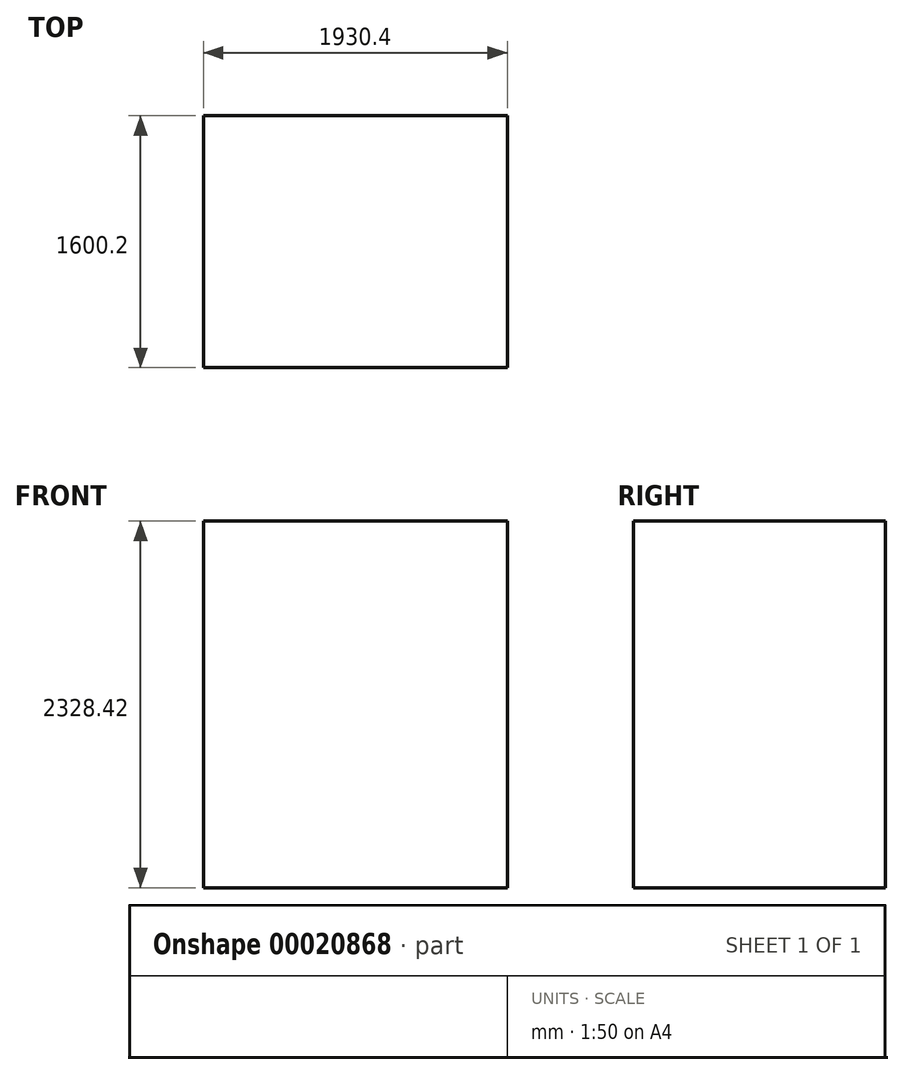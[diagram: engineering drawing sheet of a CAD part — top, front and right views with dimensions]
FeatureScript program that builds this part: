
annotation { "Feature Type Name" : "Feature", "Feature Type Description" : "" }
export const myFeature = defineFeature(function(context is Context, id is Id, definition is map)
    precondition{}
    {
        {
            var Q0;
            Q0=qCreatedBy(makeId("Top.planeOp"),FACE);
            var sketch = newSketch(context, id + "F0", { "sketchPlane" : qUnion([Q0])});
            skLineSegment(sketch, "E0", {"start": v(0, 0) * mm, "end": v(-1930.4, 0) * mm});
            skLineSegment(sketch, "E1", {"start": v(-1930.4, 0) * mm, "end": v(-1930.4, -1600.2) * mm});
            skLineSegment(sketch, "E2", {"start": v(-1930.4, -1600.2) * mm, "end": v(0, -1600.2) * mm});
            skLineSegment(sketch, "E3", {"start": v(0, 0) * mm, "end": v(0, -1600.2) * mm});
            skSolve(sketch);
        }
        {
            var Q0;
            Q0=makeQuery(id+"F0.imprint","IMPRINT",FACE,{"disambiguationData":[TD([[makeQuery(id+"F0.imprint","IMPRINT",EDGE,{"derivedFrom":sQuery(id+"F0.wireOp",EDGE,"E0")}),1.0]])]});
            extrude(context, id + "F1", {"entities" : qUnion([Q0]), "depth" : 2328.42 * mm});
        }
    });
